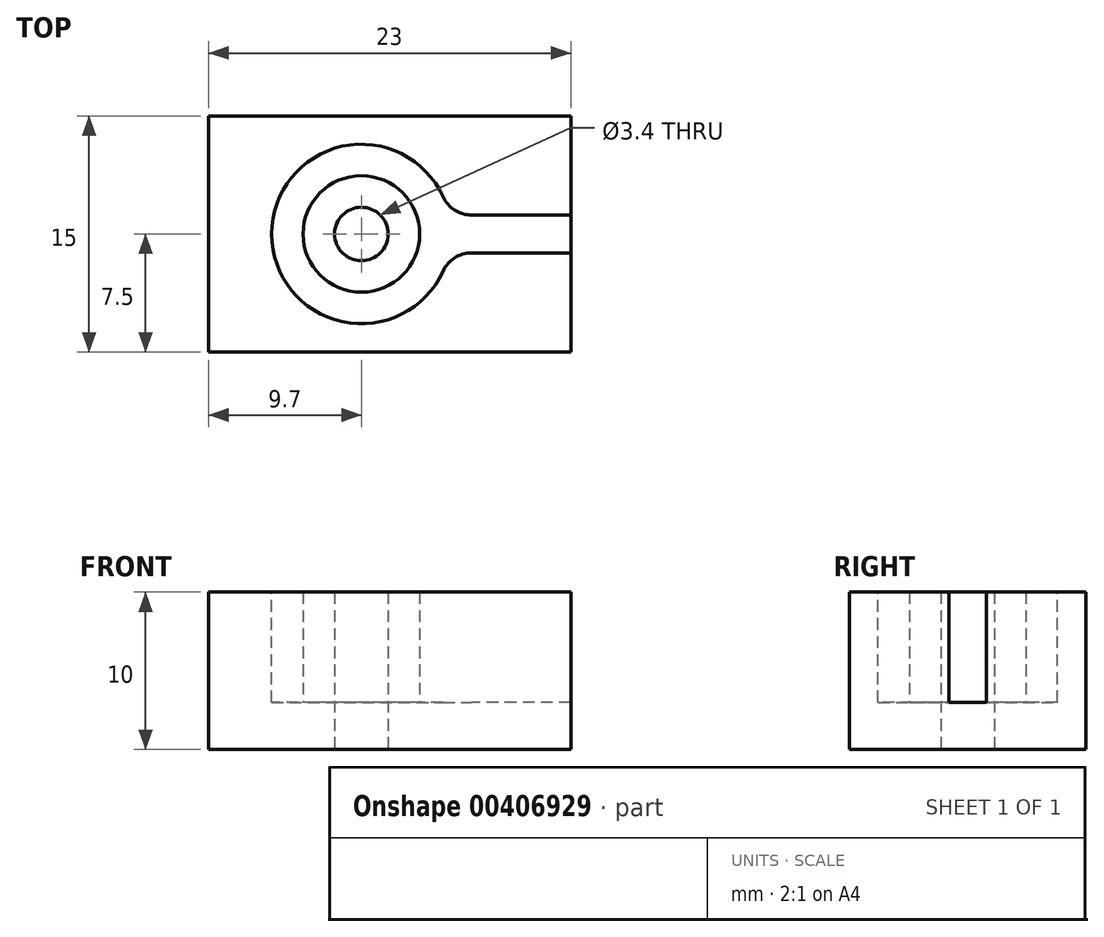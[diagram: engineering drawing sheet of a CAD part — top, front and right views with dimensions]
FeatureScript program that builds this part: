
annotation { "Feature Type Name" : "Feature", "Feature Type Description" : "" }
export const myFeature = defineFeature(function(context is Context, id is Id, definition is map)
    precondition{}
    {
        {
            var Q0;
            Q0=qCreatedBy(makeId("Top.planeOp"),FACE);
            var sketch = newSketch(context, id + "F0", { "sketchPlane" : qUnion([Q0])});
            skCircle(sketch, "E0", {"center": v(0, 0) * mm, "radius": 1.7 * mm});
            skCircle(sketch, "E1", {"center": v(0, 0) * mm, "radius": 3.7 * mm});
            skCircle(sketch, "E2", {"center": v(0, 0) * mm, "radius": 5.7 * mm});
            skSolve(sketch);
        }
        {
            var Q0;
            Q0=qCreatedBy(makeId("Top.planeOp"),FACE);
            var sketch = newSketch(context, id + "F1", { "sketchPlane" : qUnion([Q0])});
            skLineSegment(sketch, "E3.bottom", {"start": v(13.3, -7.5) * mm, "end": v(-9.7, -7.5) * mm});
            skLineSegment(sketch, "E3.top", {"start": v(13.3, 7.5) * mm, "end": v(-9.7, 7.5) * mm});
            skLineSegment(sketch, "E3.left", {"start": v(13.3, -7.5) * mm, "end": v(13.3, 7.5) * mm});
            skLineSegment(sketch, "E3.right", {"start": v(-9.7, -7.5) * mm, "end": v(-9.7, 7.5) * mm});
            skPoint(sketch, "E3.middle", {"position": v(1.8, 0) * mm});
            skSolve(sketch);
        }
        {
            var Q0;
            Q0 = qSketchRegion(id + "F1", true);
            extrude(context, id + "F2", {"entities" : qUnion([Q0]), "depth" : 10 * mm});
        }
        {
            var Q0;
            Q0=makeQuery(id+"F2.opExtrude","CAP_FACE",FACE,{"disambiguationData":[OSD([sQuery(id+"F1.wireOp",EDGE,"E3.bottom"),sQuery(id+"F1.wireOp",EDGE,"E3.top"),sQuery(id+"F1.wireOp",EDGE,"E3.left"),sQuery(id+"F1.wireOp",EDGE,"E3.right")])],"isStart":false});
            var sketch = newSketch(context, id + "F3", { "sketchPlane" : qUnion([Q0])});
            skCircle(sketch, "E4", {"center": v(0, 0) * mm, "radius": 5.7 * mm});
            skLineSegment(sketch, "E5.bottom", {"start": v(15.83, -1.2) * mm, "end": v(1.57, -1.2) * mm});
            skLineSegment(sketch, "E5.top", {"start": v(15.83, 1.2) * mm, "end": v(1.57, 1.2) * mm});
            skLineSegment(sketch, "E5.left", {"start": v(15.83, -1.2) * mm, "end": v(15.83, 1.2) * mm});
            skLineSegment(sketch, "E5.right", {"start": v(1.57, -1.2) * mm, "end": v(1.57, 1.2) * mm});
            skPoint(sketch, "E5.middle", {"position": v(8.7, 0) * mm});
            skSolve(sketch);
        }
        {
            var Q0;
            Q0 = qSketchRegion(id + "F3", true);
            extrude(context, id + "F4", {"entities" : qUnion([Q0]), "operationType" : NewBodyOperationType.REMOVE, "oppositeDirection" : true, "depth" : 7 * mm});
        }
        {
            var Q0;
            Q0=makeQuery(id+"F4.boolean.opBoolean","COPY",EDGE,{"derivedFrom":makeQuery(id+"F4.opExtrude","SWEPT_EDGE",EDGE,{"disambiguationData":[OSD([sQuery(id+"F3.wireOp",EDGE,"E4"),sQuery(id+"F3.wireOp",EDGE,"E5.top")])]})});
            var Q1;
            Q1=makeQuery(id+"F4.boolean.opBoolean","COPY",EDGE,{"derivedFrom":makeQuery(id+"F4.opExtrude","SWEPT_EDGE",EDGE,{"disambiguationData":[OSD([sQuery(id+"F3.wireOp",EDGE,"E4"),sQuery(id+"F3.wireOp",EDGE,"E5.bottom")])]})});
            fillet(context, id + "F5", {"entities" : qUnion([Q0, Q1]), "radius" : 2 * mm, "tangentPropagation" : true, "allowEdgeOverflow" : false});
        }
        {
            var Q0;
            Q0=makeQuery(id+"F4.boolean.opBoolean","COPY",FACE,{"derivedFrom":makeQuery(id+"F4.opExtrude","CAP_FACE",FACE,{"disambiguationData":[OSD([sQuery(id+"F3.wireOp",EDGE,"E4"),sQuery(id+"F3.wireOp",EDGE,"E5.bottom"),sQuery(id+"F3.wireOp",EDGE,"E5.top"),sQuery(id+"F3.wireOp",EDGE,"E5.left")])],"isStart":false})});
            var sketch = newSketch(context, id + "F6", { "sketchPlane" : qUnion([Q0])});
            skCircle(sketch, "E6", {"center": v(0, 0) * mm, "radius": 3.7 * mm});
            skCircle(sketch, "E7", {"center": v(0, 0) * mm, "radius": 1.7 * mm});
            skSolve(sketch);
        }
        {
            var Q0;
            Q0 = qSketchRegion(id + "F6", true);
            extrude(context, id + "F7", {"entities" : qUnion([Q0]), "operationType" : NewBodyOperationType.ADD, "depth" : 7 * mm});
        }
        {
            var Q0;
            Q0=makeQuery(id+"F7.boolean.opBoolean","SPLIT",FACE,{"disambiguationData":[TD([makeQuery(id+"F7.opExtrude","SWEPT_FACE",FACE,{"disambiguationData":[OSD([sQuery(id+"F6.wireOp",EDGE,"E7")])]})])],"derivedFrom":makeQuery(id+"F4.boolean.opBoolean","COPY",FACE,{"derivedFrom":makeQuery(id+"F4.opExtrude","CAP_FACE",FACE,{"disambiguationData":[OSD([sQuery(id+"F3.wireOp",EDGE,"E4"),sQuery(id+"F3.wireOp",EDGE,"E5.bottom"),sQuery(id+"F3.wireOp",EDGE,"E5.top"),sQuery(id+"F3.wireOp",EDGE,"E5.left")])],"isStart":false})})});
            extrude(context, id + "F8", {"entities" : qUnion([Q0]), "operationType" : NewBodyOperationType.REMOVE, "oppositeDirection" : true, "depth" : 25 * mm});
        }
    });
